# Revit family: NTO_Seating_TrufflePouf
name_source: partatom
category: Furniture
units: mm (PartAtom-declared; Revit-internal decimal feet)

## family parameters
Always vertical = Yes
Cut with Voids When Loaded = No
OmniClass Number = 23.40.50.11.14
OmniClass Title = Classroom Furniture
Room Calculation Point = No
Shared = Yes
Work Plane-Based = No

## types (2) — shared parameters
Assembly Code = E2020200
AssetType = Movable
Category = Pr_40_50_12_83 : Stacking chairs
CodePerformance = Certified under UK standard BS EN 1729 (Parts 1&2) by FIRA.
Color = Upholstery
Upholstery
Description = Seating_TrufflePoufe
DurationUnit = year
ExpectedLife = 10
Features = Upholstery
Upholstery
Finish = Upholstery
Upholstery
Hardware = NTO_Generic_Plastic_LightSand
IfcExportAs = IfcFurnishingElementType
IfcExportType = CHAIR
Keynote = Pr_40_50_12_83
MainColor = Upholstery
Upholstery
ManufacturerName = Naughtone
Material = Upholstery
Upholstery
ModelReference = Seating_TrufflePoufe
NBSDescription = Seating
NBSReference = 45-35-72/352
Shape = Circular
Uniclass2015Code = Pr_40_50_12_83
Uniclass2015Title = Stacking chairs
Uniclass2015Version = Products v1.10
Version = 1
WarrantyDescription = 10 years
WarrantyDurationLabor = 10
WarrantyDurationParts = 10
WarrantyDurationUnit = Years
zero-valued in all types: Cost, Default Elevation

## per-type parameters (varying)
| type | AccessibilityPerformance | BIMObjectName | ManufacturerURL | Name | NominalHeight | NominalLength | NominalWidth | ProductInformation | Size | SustainabilityPerformance | TrouflePoufeA | TrufflePoufeB | Type Comments | URL | Upholstery |
| NOTRFB |  | NTO_Seating_TrufflePouf_NOTRFB | www.kieurope.com | Seating_TrufflePoufe_NOTRFB | 760 mm | 480 mm | 505 mm | www.kieurope.com/Postura | 475 x 465 x 445 mm | 100% recyclable | No | Yes | 475 x 465 x 445 mm | https://www.naughtone.com | NTO_Upholstery_Fabric_Beige |
| NOTRFA | BS 5852: 2006 Clause 12 Ignition Sources 0. 1 & 5 (Crib5) | NTO_Seating_TrufflePouf_NOTRFA | www.NaughtOne.com | Seating_TurfflePoufe_NOTRFA | 400 mm  [stored 1.31234 ft] | 605 mm | 600 mm | www.NaughtOne.com/Truffle | 605 x 600 x 400 mm |  | Yes | No | 605 x 600 x 400 mm | www.NaughtOne.com | NTO_Upholstery_Fabric_InkBlue |

note: column(s) folded — value = type name in every type: Model, ModelNumber

note: [stored X ft] marks values corroborated as IEEE doubles in the binary element streams (Revit-internal decimal feet)

## geometry (parser evidence)
native form markers: Sweep x3
no freeform markers — native parametric forms only
